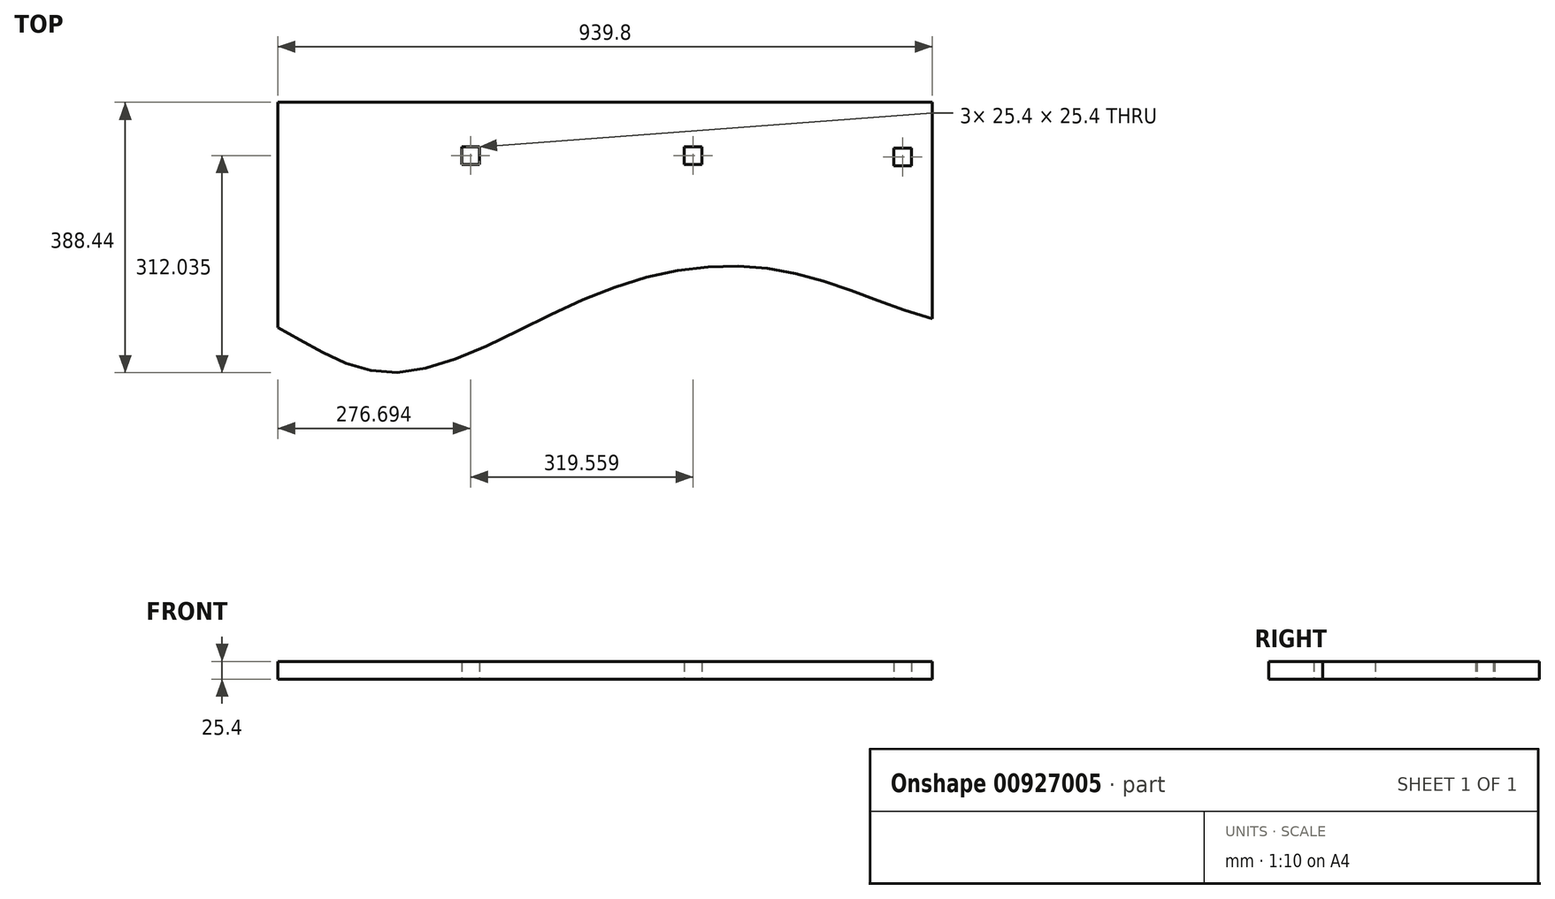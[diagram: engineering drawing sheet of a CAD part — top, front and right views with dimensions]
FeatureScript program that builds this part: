
annotation { "Feature Type Name" : "Feature", "Feature Type Description" : "" }
export const myFeature = defineFeature(function(context is Context, id is Id, definition is map)
    precondition{}
    {
        {
            var Q0;
            Q0=qCreatedBy(makeId("Top.planeOp"),FACE);
            var sketch = newSketch(context, id + "F0", { "sketchPlane" : qUnion([Q0])});
            skLineSegment(sketch, "E0.bottom", {"start": v(513.45, 553.4) * mm, "end": v(818.25, 553.4) * mm});
            skLineSegment(sketch, "E0.top", {"start": v(513.45, 832.8) * mm, "end": v(818.25, 832.8) * mm});
            skLineSegment(sketch, "E0.left", {"start": v(513.45, 553.4) * mm, "end": v(513.45, 832.8) * mm});
            skLineSegment(sketch, "E0.right", {"start": v(818.25, 553.4) * mm, "end": v(818.25, 832.8) * mm});
            skLineSegment(sketch, "E1", {"start": v(818.25, 832.8) * mm, "end": v(1377.05, 832.8) * mm});
            skLineSegment(sketch, "E2", {"start": v(1377.05, 832.8) * mm, "end": v(1377.05, 553.4) * mm});
            skLineSegment(sketch, "E3", {"start": v(1377.05, 553.4) * mm, "end": v(818.25, 553.4) * mm});
            skLineSegment(sketch, "E4", {"start": v(1377.05, 832.8) * mm, "end": v(1758.05, 832.8) * mm});
            skLineSegment(sketch, "E5", {"start": v(1758.05, 832.8) * mm, "end": v(1758.05, 553.4) * mm});
            skLineSegment(sketch, "E6", {"start": v(1758.05, 553.4) * mm, "end": v(1377.05, 553.4) * mm});
            skLineSegment(sketch, "E7", {"start": v(513.45, 832.8) * mm, "end": v(818.25, 553.4) * mm, "construction": true});
            skLineSegment(sketch, "E8", {"start": v(818.25, 832.8) * mm, "end": v(513.45, 553.4) * mm, "construction": true});
            skLineSegment(sketch, "E9", {"start": v(1377.05, 832.8) * mm, "end": v(1758.05, 553.4) * mm, "construction": true});
            skLineSegment(sketch, "E10", {"start": v(1377.05, 553.4) * mm, "end": v(1758.05, 832.8) * mm, "construction": true});
            skLineSegment(sketch, "E11", {"start": v(818.25, 553.4) * mm, "end": v(818.25, 230.04) * mm});
            skLineSegment(sketch, "E12", {"start": v(1758.05, 242.42) * mm, "end": v(1758.05, 553.4) * mm});
            skFitSpline(sketch, "E13", {"points": [v(818.25, 230.04) * mm, v(988.58, 165.04) * mm, v(1276.45, 278.02) * mm, v(1538, 312.07) * mm, v(1758.05, 242.42) * mm], "startDerivative": vector(715.35, -402.32) * mm, "endDerivative": vector(905.53, -253.27) * mm});
            skLineSegment(sketch, "E14", {"start": v(513.45, 553.4) * mm, "end": v(513.45, 451.8) * mm});
            skLineSegment(sketch, "E15", {"start": v(513.45, 451.8) * mm, "end": v(1758.05, 451.8) * mm, "construction": true});
            skLineSegment(sketch, "E16.bottom", {"start": v(533.89, 488.25) * mm, "end": v(559.29, 488.25) * mm});
            skLineSegment(sketch, "E16.top", {"start": v(533.89, 462.85) * mm, "end": v(559.29, 462.85) * mm});
            skLineSegment(sketch, "E16.left", {"start": v(533.89, 488.25) * mm, "end": v(533.89, 462.85) * mm});
            skLineSegment(sketch, "E16.right", {"start": v(559.29, 488.25) * mm, "end": v(559.29, 462.85) * mm});
            skLineSegment(sketch, "E17", {"start": v(533.89, 488.25) * mm, "end": v(559.29, 462.85) * mm});
            skLineSegment(sketch, "E18", {"start": v(559.29, 488.25) * mm, "end": v(533.89, 462.85) * mm});
            skLineSegment(sketch, "E19.bottom", {"start": v(773.78, 489.44) * mm, "end": v(799.18, 489.44) * mm});
            skLineSegment(sketch, "E19.top", {"start": v(773.78, 464.04) * mm, "end": v(799.18, 464.04) * mm});
            skLineSegment(sketch, "E19.left", {"start": v(773.78, 489.44) * mm, "end": v(773.78, 464.04) * mm});
            skLineSegment(sketch, "E19.right", {"start": v(799.18, 489.44) * mm, "end": v(799.18, 464.04) * mm});
            skLineSegment(sketch, "E20", {"start": v(773.78, 489.44) * mm, "end": v(799.18, 464.04) * mm});
            skLineSegment(sketch, "E21", {"start": v(799.18, 489.44) * mm, "end": v(773.78, 464.04) * mm});
            skLineSegment(sketch, "E22.bottom", {"start": v(1082.24, 489.7) * mm, "end": v(1107.64, 489.7) * mm});
            skLineSegment(sketch, "E22.top", {"start": v(1082.24, 464.3) * mm, "end": v(1107.64, 464.3) * mm});
            skLineSegment(sketch, "E22.left", {"start": v(1082.24, 489.7) * mm, "end": v(1082.24, 464.3) * mm});
            skLineSegment(sketch, "E22.right", {"start": v(1107.64, 489.7) * mm, "end": v(1107.64, 464.3) * mm});
            skLineSegment(sketch, "E23", {"start": v(1082.24, 489.7) * mm, "end": v(1107.64, 464.3) * mm});
            skLineSegment(sketch, "E24", {"start": v(1107.64, 489.7) * mm, "end": v(1082.24, 464.3) * mm});
            skLineSegment(sketch, "E25.bottom", {"start": v(1401.8, 489.7) * mm, "end": v(1427.2, 489.7) * mm});
            skLineSegment(sketch, "E25.top", {"start": v(1401.8, 464.3) * mm, "end": v(1427.2, 464.3) * mm});
            skLineSegment(sketch, "E25.left", {"start": v(1401.8, 489.7) * mm, "end": v(1401.8, 464.3) * mm});
            skLineSegment(sketch, "E25.right", {"start": v(1427.2, 489.7) * mm, "end": v(1427.2, 464.3) * mm});
            skLineSegment(sketch, "E26", {"start": v(1401.8, 489.7) * mm, "end": v(1427.2, 464.3) * mm});
            skLineSegment(sketch, "E27", {"start": v(1427.2, 489.7) * mm, "end": v(1401.8, 464.3) * mm});
            skLineSegment(sketch, "E28.bottom", {"start": v(1702.76, 487.52) * mm, "end": v(1728.16, 487.52) * mm});
            skLineSegment(sketch, "E28.top", {"start": v(1702.76, 462.12) * mm, "end": v(1728.16, 462.12) * mm});
            skLineSegment(sketch, "E28.left", {"start": v(1702.76, 487.52) * mm, "end": v(1702.76, 462.12) * mm});
            skLineSegment(sketch, "E28.right", {"start": v(1728.16, 487.52) * mm, "end": v(1728.16, 462.12) * mm});
            skLineSegment(sketch, "E29", {"start": v(1702.76, 487.52) * mm, "end": v(1728.16, 462.12) * mm});
            skLineSegment(sketch, "E30", {"start": v(1728.16, 487.52) * mm, "end": v(1702.76, 462.12) * mm});
            skLineSegment(sketch, "E31.bottom", {"start": v(-12.7, 12.7) * mm, "end": v(12.7, 12.7) * mm});
            skLineSegment(sketch, "E31.top", {"start": v(-12.7, -12.7) * mm, "end": v(12.7, -12.7) * mm});
            skLineSegment(sketch, "E31.left", {"start": v(-12.7, 12.7) * mm, "end": v(-12.7, -12.7) * mm});
            skLineSegment(sketch, "E31.right", {"start": v(12.7, 12.7) * mm, "end": v(12.7, -12.7) * mm});
            skLineSegment(sketch, "E32", {"start": v(-12.7, 12.7) * mm, "end": v(12.7, -12.7) * mm});
            skLineSegment(sketch, "E33", {"start": v(12.7, 12.7) * mm, "end": v(-12.7, -12.7) * mm});
            skSolve(sketch);
        }
        {
            var Q0;
            Q0=makeQuery(id+"F0.imprint","IMPRINT",FACE,{"disambiguationData":[TD([[makeQuery(id+"F0.imprint","IMPRINT",EDGE,{"derivedFrom":sQuery(id+"F0.wireOp",EDGE,"E3")}),1.0]])]});
            extrude(context, id + "F1", {"entities" : qUnion([Q0]), "depth" : 25.4 * mm, "offsetDistance" : 25.4 * mm});
        }
    });
